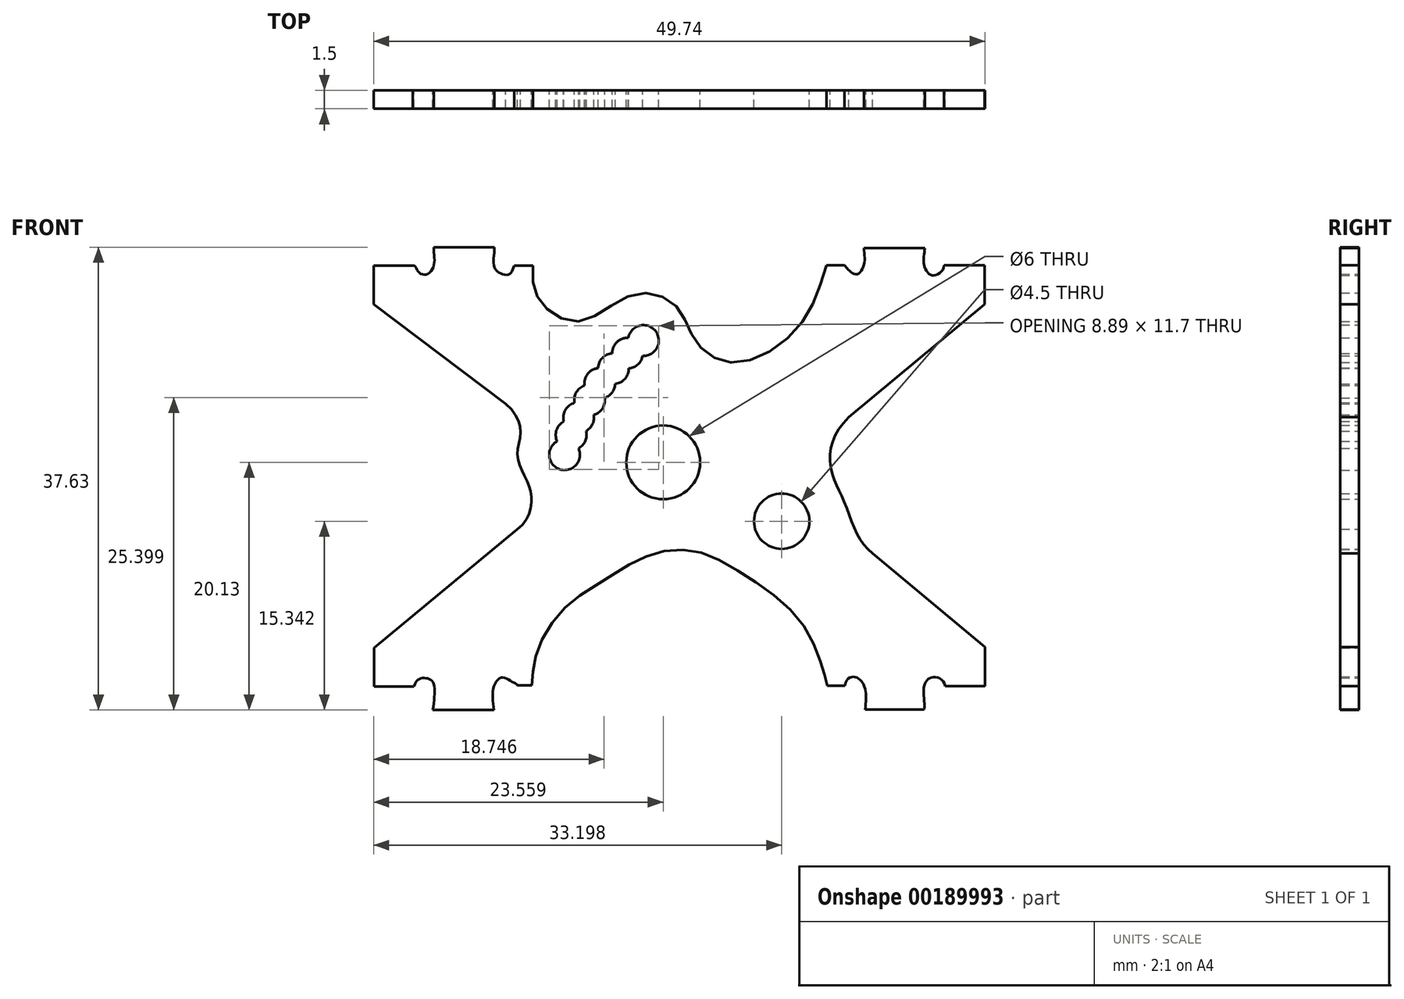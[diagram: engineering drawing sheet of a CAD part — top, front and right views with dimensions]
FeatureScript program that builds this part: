
annotation { "Feature Type Name" : "Feature", "Feature Type Description" : "" }
export const myFeature = defineFeature(function(context is Context, id is Id, definition is map)
    precondition{}
    {
        {
            var Q0;
            Q0=qCreatedBy(makeId("Front.planeOp"),FACE);
            var sketch = newSketch(context, id + "F0", { "sketchPlane" : qUnion([Q0])});
            skLineSegment(sketch, "E0", {"start": v(-19.95, 17.36) * mm, "end": v(-15.03, 17.36) * mm});
            skLineSegment(sketch, "E1", {"start": v(-13.4, 15.85) * mm, "end": v(-11.9, 15.85) * mm});
            skLineSegment(sketch, "E2", {"start": v(-24.85, 15.87) * mm, "end": v(-21.65, 15.87) * mm});
            skLineSegment(sketch, "E3", {"start": v(-24.85, 15.87) * mm, "end": v(-24.85, 12.7) * mm});
            skLineSegment(sketch, "E4", {"start": v(12, 15.9) * mm, "end": v(13.46, 15.9) * mm});
            skLineSegment(sketch, "E5", {"start": v(15.03, 17.3) * mm, "end": v(20, 17.3) * mm});
            skLineSegment(sketch, "E6", {"start": v(21.55, 15.88) * mm, "end": v(24.85, 15.88) * mm});
            skLineSegment(sketch, "E7", {"start": v(24.85, 15.88) * mm, "end": v(24.85, 12.7) * mm});
            skLineSegment(sketch, "E8", {"start": v(24.85, 12.7) * mm, "end": v(13.8, 3.53) * mm});
            skLineSegment(sketch, "E9", {"start": v(-24.85, 12.7) * mm, "end": v(-14.1, 4.62) * mm});
            skLineSegment(sketch, "E10", {"start": v(-21.55, -18.36) * mm, "end": v(-24.82, -18.36) * mm});
            skLineSegment(sketch, "E11", {"start": v(-24.82, -18.36) * mm, "end": v(-24.82, -15.24) * mm});
            skLineSegment(sketch, "E12", {"start": v(-24.82, -15.24) * mm, "end": v(-13.16, -5.58) * mm});
            skLineSegment(sketch, "E13", {"start": v(-20.03, -20.27) * mm, "end": v(-15.06, -20.27) * mm});
            skLineSegment(sketch, "E14", {"start": v(-11.97, -18.26) * mm, "end": v(-13.14, -18.26) * mm});
            skLineSegment(sketch, "E15", {"start": v(12.07, -18.3) * mm, "end": v(13.5, -18.3) * mm});
            skLineSegment(sketch, "E16", {"start": v(15.13, -20.23) * mm, "end": v(19.94, -20.23) * mm});
            skLineSegment(sketch, "E17", {"start": v(21.66, -18.33) * mm, "end": v(24.89, -18.33) * mm});
            skLineSegment(sketch, "E18", {"start": v(24.89, -18.33) * mm, "end": v(24.89, -15.17) * mm});
            skLineSegment(sketch, "E19", {"start": v(24.89, -15.17) * mm, "end": v(15.74, -7.55) * mm});
            skPoint(sketch, "E20", {"position": v(-1.3, 0) * mm});
            skPoint(sketch, "E21", {"position": v(8.35, -4.84) * mm});
            skPoint(sketch, "E22", {"position": v(-2.9, 9.77) * mm});
            skPoint(sketch, "E23", {"position": v(-4.19, 8.74) * mm});
            skPoint(sketch, "E24", {"position": v(-5.34, 7.48) * mm});
            skPoint(sketch, "E25", {"position": v(-6.44, 6.29) * mm});
            skPoint(sketch, "E26", {"position": v(-7.28, 4.92) * mm});
            skPoint(sketch, "E27", {"position": v(-8.17, 3.5) * mm});
            skPoint(sketch, "E28", {"position": v(-8.78, 2.1) * mm});
            skPoint(sketch, "E29", {"position": v(-9.3, 0.49) * mm});
            skCircle(sketch, "E30", {"center": v(-1.3, -0.14) * mm, "radius": 3 * mm});
            skCircle(sketch, "E31", {"center": v(8.35, -4.93) * mm, "radius": 2.25 * mm});
            skArc(sketch, "E32", {"start": v(-2.96, 8.52) * mm, "mid": v(-1.92, 10.55) * mm, "end": v(-4.13, 9.99) * mm});
            skArc(sketch, "E33", {"start": v(-4.13, 9.99) * mm, "mid": v(-5.06, 9.64) * mm, "end": v(-5.44, 8.73) * mm});
            skArc(sketch, "E34", {"start": v(-5.44, 8.73) * mm, "mid": v(-6.24, 8.35) * mm, "end": v(-6.59, 7.53) * mm});
            skArc(sketch, "E35", {"start": v(-6.59, 7.53) * mm, "mid": v(-7.44, 7.05) * mm, "end": v(-7.68, 6.1) * mm});
            skArc(sketch, "E36", {"start": v(-7.68, 6.1) * mm, "mid": v(-8.35, 5.56) * mm, "end": v(-8.5, 4.7) * mm});
            skArc(sketch, "E37", {"start": v(-8.5, 4.7) * mm, "mid": v(-9.25, 4.12) * mm, "end": v(-9.38, 3.19) * mm});
            skArc(sketch, "E38", {"start": v(-9.38, 3.19) * mm, "mid": v(-9.96, 2.49) * mm, "end": v(-9.92, 1.58) * mm});
            skArc(sketch, "E39", {"start": v(-9.92, 1.58) * mm, "mid": v(-9.7, -0.7) * mm, "end": v(-8.17, 1) * mm});
            skPoint(sketch, "E40", {"position": v(-20.63, 15.13) * mm});
            skPoint(sketch, "E41", {"position": v(-14.57, 15.25) * mm});
            skPoint(sketch, "E42", {"position": v(-11.2, 12.85) * mm});
            skPoint(sketch, "E43", {"position": v(-8, 11.34) * mm});
            skPoint(sketch, "E44", {"position": v(-3.87, 13.46) * mm});
            skPoint(sketch, "E45", {"position": v(-0.32, 12.66) * mm});
            skPoint(sketch, "E46", {"position": v(1.38, 9.68) * mm});
            skPoint(sketch, "E47", {"position": v(4.55, 7.97) * mm});
            skPoint(sketch, "E48", {"position": v(9.62, 10.77) * mm});
            skPoint(sketch, "E49", {"position": v(14.47, 15.16) * mm});
            skPoint(sketch, "E50", {"position": v(20.63, 15.07) * mm});
            skPoint(sketch, "E51", {"position": v(12.35, 1.04) * mm});
            skPoint(sketch, "E52", {"position": v(12.54, -1.33) * mm});
            skPoint(sketch, "E53", {"position": v(13.38, -3.22) * mm});
            skPoint(sketch, "E54", {"position": v(14.36, -5.73) * mm});
            skPoint(sketch, "E55", {"position": v(20.64, -17.62) * mm});
            skPoint(sketch, "E56", {"position": v(14.3, -17.6) * mm});
            skPoint(sketch, "E57", {"position": v(11.61, -16.64) * mm});
            skPoint(sketch, "E58", {"position": v(9.72, -12.85) * mm});
            skPoint(sketch, "E59", {"position": v(5.52, -9.42) * mm});
            skPoint(sketch, "E60", {"position": v(1.31, -7.36) * mm});
            skPoint(sketch, "E61", {"position": v(-2.54, -7.74) * mm});
            skPoint(sketch, "E62", {"position": v(-6.23, -9.8) * mm});
            skPoint(sketch, "E63", {"position": v(-9.63, -12.3) * mm});
            skPoint(sketch, "E64", {"position": v(-11.65, -15.9) * mm});
            skPoint(sketch, "E65", {"position": v(-14.38, -17.63) * mm});
            skPoint(sketch, "E66", {"position": v(-20.74, -17.68) * mm});
            skPoint(sketch, "E67", {"position": v(-12, -3.45) * mm});
            skPoint(sketch, "E68", {"position": v(-12.39, -1.62) * mm});
            skPoint(sketch, "E69", {"position": v(-13.14, 0.36) * mm});
            skPoint(sketch, "E70", {"position": v(-12.9, 2.3) * mm});
            skFitSpline(sketch, "E71", {"points": [v(-14.1, 4.62) * mm, v(-12.9, 2.3) * mm, v(-13.14, 0.36) * mm, v(-12.39, -1.62) * mm, v(-12, -3.45) * mm, v(-13.16, -5.58) * mm], "startDerivative": vector(12.13, -10.26) * mm, "endDerivative": vector(-10.89, -7.64) * mm});
            skFitSpline(sketch, "E72", {"points": [v(-21.55, -18.36) * mm, v(-20.74, -17.68) * mm, v(-20.03, -18) * mm, v(-20.03, -20.27) * mm], "startDerivative": vector(1.9, 5.9) * mm, "endDerivative": vector(-0.84, -5.97) * mm});
            skFitSpline(sketch, "E73", {"points": [v(-15.06, -20.27) * mm, v(-15.06, -18.36) * mm, v(-14.38, -17.63) * mm, v(-13.64, -17.95) * mm, v(-13.14, -18.26) * mm], "startDerivative": vector(-0.74, 5.84) * mm, "endDerivative": vector(1.36, -1.78) * mm});
            skFitSpline(sketch, "E74", {"points": [v(-11.97, -18.26) * mm, v(-11.65, -15.9) * mm, v(-9.63, -12.3) * mm, v(-6.23, -9.8) * mm, v(-2.54, -7.74) * mm, v(1.31, -7.36) * mm, v(5.52, -9.42) * mm, v(9.72, -12.85) * mm, v(11.61, -16.64) * mm, v(12.07, -18.3) * mm], "startDerivative": vector(0.88, 25.13) * mm, "endDerivative": vector(4.71, -19.69) * mm});
            skFitSpline(sketch, "E75", {"points": [v(13.5, -18.3) * mm, v(14.3, -17.6) * mm, v(15.08, -18.36) * mm, v(15.13, -20.23) * mm], "startDerivative": vector(0.94, 6.1) * mm, "endDerivative": vector(-0.59, -5) * mm});
            skFitSpline(sketch, "E76", {"points": [v(19.94, -20.23) * mm, v(19.94, -18.3) * mm, v(20.64, -17.62) * mm, v(21.66, -18.33) * mm], "startDerivative": vector(0.51, 5.23) * mm, "endDerivative": vector(1.1, -5.22) * mm});
            skFitSpline(sketch, "E77", {"points": [v(15.74, -7.55) * mm, v(14.36, -5.73) * mm, v(13.38, -3.22) * mm, v(12.54, -1.33) * mm, v(12.35, 1.04) * mm, v(13.8, 3.53) * mm], "startDerivative": vector(-9.76, 8.3) * mm, "endDerivative": vector(11.04, 11.08) * mm});
            skFitSpline(sketch, "E78", {"points": [v(21.55, 15.88) * mm, v(20.63, 15.07) * mm, v(19.94, 15.88) * mm, v(20, 17.3) * mm], "startDerivative": vector(-0.22, -4.67) * mm, "endDerivative": vector(0.4, 3.98) * mm});
            skFitSpline(sketch, "E79", {"points": [v(15.03, 17.3) * mm, v(15.03, 15.88) * mm, v(14.47, 15.16) * mm, v(13.8, 15.48) * mm, v(13.46, 15.9) * mm], "startDerivative": vector(0.57, -4.64) * mm, "endDerivative": vector(-1.43, 2.08) * mm});
            skFitSpline(sketch, "E80", {"points": [v(12, 15.9) * mm, v(9.62, 10.77) * mm, v(4.55, 7.97) * mm, v(1.38, 9.68) * mm, v(-0.32, 12.66) * mm, v(-3.87, 13.46) * mm, v(-8, 11.34) * mm, v(-11.2, 12.85) * mm, v(-11.9, 15.85) * mm], "startDerivative": vector(-11.17, -37.06) * mm, "endDerivative": vector(3.51, 32.85) * mm});
            skFitSpline(sketch, "E81", {"points": [v(-13.4, 15.85) * mm, v(-13.8, 15.16) * mm, v(-14.57, 15.25) * mm, v(-15.06, 15.85) * mm, v(-15.03, 17.36) * mm], "startDerivative": vector(-1.5, -3.62) * mm, "endDerivative": vector(-0.17, 5.1) * mm});
            skFitSpline(sketch, "E82", {"points": [v(-19.95, 17.36) * mm, v(-19.95, 15.85) * mm, v(-20.63, 15.13) * mm, v(-21.29, 15.47) * mm, v(-21.65, 15.87) * mm], "startDerivative": vector(0, -5.14) * mm, "endDerivative": vector(-3.74, -0.23) * mm});
            skArc(sketch, "E83.trimOffspring", {"start": v(-4.09, 7.5) * mm, "mid": v(-3.35, 7.81) * mm, "end": v(-2.96, 8.52) * mm});
            skArc(sketch, "E84.trimOffspring", {"start": v(-5.2, 6.24) * mm, "mid": v(-4.4, 6.66) * mm, "end": v(-4.09, 7.5) * mm});
            skArc(sketch, "E85.trimOffspring", {"start": v(-6.04, 5.1) * mm, "mid": v(-5.44, 5.54) * mm, "end": v(-5.2, 6.24) * mm});
            skArc(sketch, "E86.trimOffspring", {"start": v(-6.94, 3.72) * mm, "mid": v(-6.23, 4.24) * mm, "end": v(-6.04, 5.1) * mm});
            skArc(sketch, "E87.trimOffspring", {"start": v(-7.57, 2.4) * mm, "mid": v(-7.04, 2.96) * mm, "end": v(-6.94, 3.72) * mm});
            skArc(sketch, "E88.trimOffspring", {"start": v(-8.17, 1) * mm, "mid": v(-7.63, 1.6) * mm, "end": v(-7.57, 2.4) * mm});
            skSolve(sketch);
        }
        {
            var Q0;
            Q0 = qSketchRegion(id + "F0", true);
            extrude(context, id + "F1", {"entities" : qUnion([Q0]), "depth" : 1.5 * mm});
        }
    });
